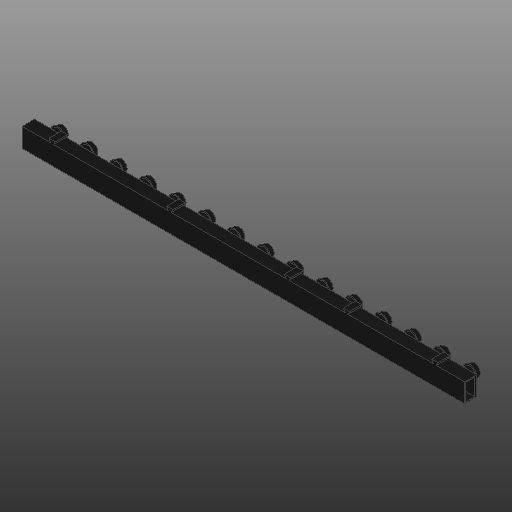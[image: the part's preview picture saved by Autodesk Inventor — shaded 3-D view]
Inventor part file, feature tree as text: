
AUTODESK INVENTOR PART (.ipt)
format: ipt  version: 2020 (Build 240168000, 168)  size: 283,136 bytes
history: native  units: in
note: dims shown in document units (in); Inventor stores cm internally (conversion verified against a paired STEP export)
features: other x6, extrude x3, pattern_linear x1, projected_geometry x1
ambient origin geometry x8: Origin, YZ Plane, XZ Plane, XY Plane, X Axis, Y Axis, Z Axis, Center Point
bodies: Solid1 (feature_tree)
feature tree (11):
  extrude  "Box"  Depth=0.0315in
  other  "Fitting Plane"
  other  "Fitting"
  extrude  "Fitting Entrance"  Depth=0.0157in
  pattern_linear  "Channel Repetition"  Spacing1=0.0157in  [1 undecoded]
  extrude  "Tabs"  Depth=0.4882in TaperAngle=0.0deg
  other  "Box Sketch"
  other  "Fitting Sketch"
  other  "Fitting Entrance Sketch"
  projected_geometry  "Projected Loop1"
  other  "Tab Sketch"
note: 1 required parameter value undecoded (feature->parameter linkage not recoverable at this tier; creation-order binding heuristic only, values carry confidence <= 0.55)
